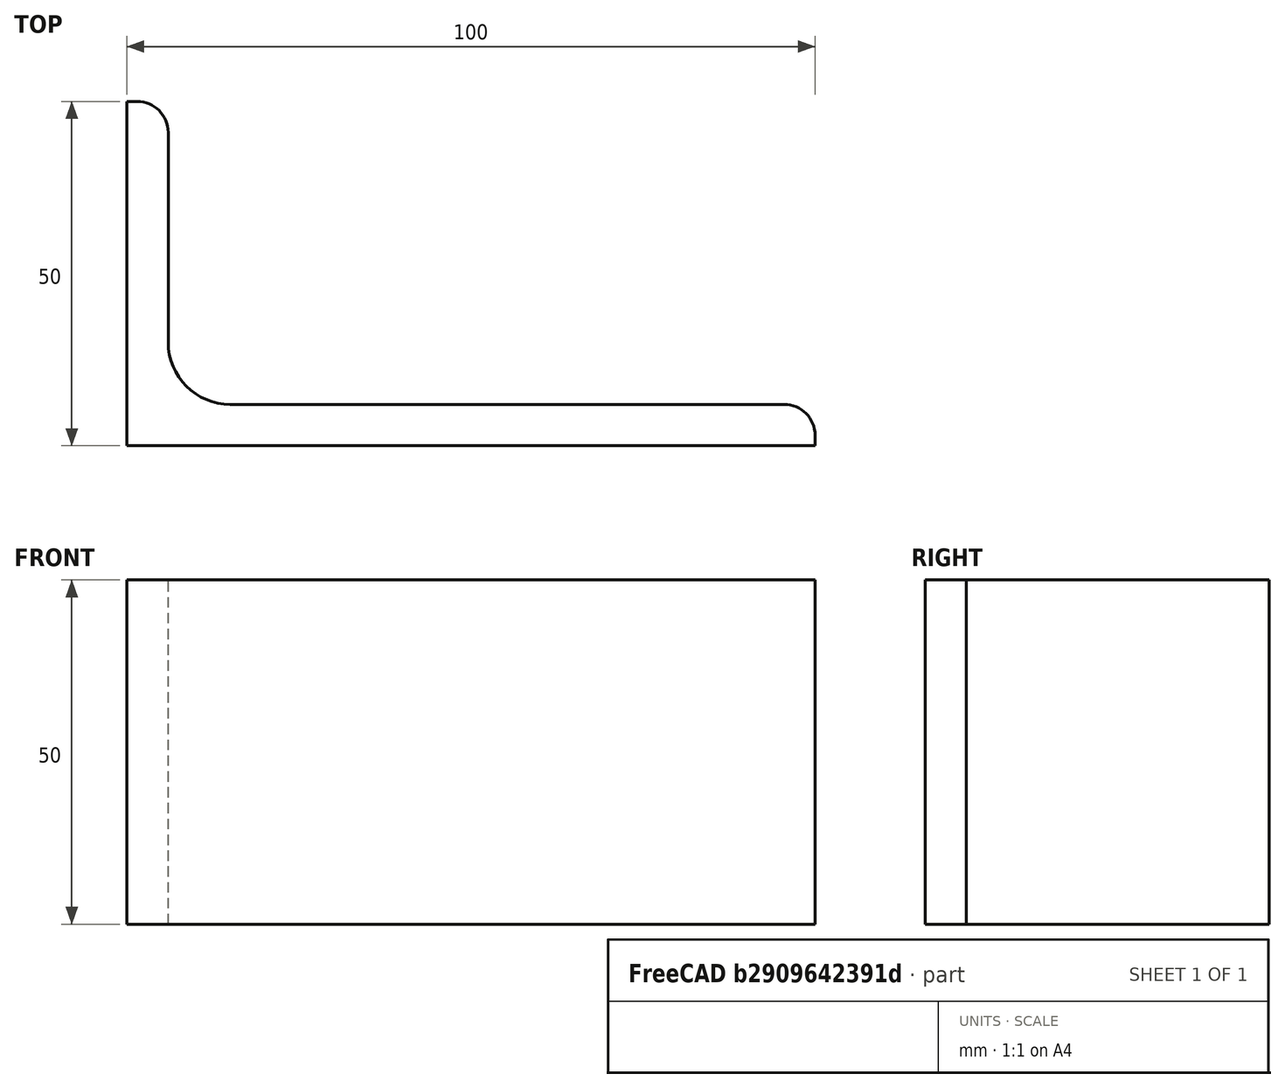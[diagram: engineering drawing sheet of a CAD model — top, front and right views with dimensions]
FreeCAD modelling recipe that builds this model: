
FCSTD DOCUMENT  (FreeCAD 0.15R4671 (Git))
Label: Angle Bar 100x50x6 EN10056 S235JR
License: All rights reserved
LicenseURL: http://en.wikipedia.org/wiki/All_rights_reserved
objects: Sketcher::SketchObject×1, Part::Extrusion×1
note: 2 computed .brp shape members not serialized (recipe doc carries the construction recipe); baked Part::Feature solids carry a one-line shape summary decoded from their .brp

FEATURE [Sketcher::SketchObject] Sketch
  sketch-geometry (9):
    g0: LineSegment StartX=0 StartY=0 StartZ=0 EndX=100 EndY=0 EndZ=0
    g1: LineSegment StartX=100 StartY=0 StartZ=0 EndX=100 EndY=1.5 EndZ=0
    g2: LineSegment StartX=95.5 StartY=6 StartZ=0 EndX=15 EndY=6 EndZ=0
    g3: LineSegment StartX=0 StartY=0 StartZ=0 EndX=0 EndY=50 EndZ=0
    g4: LineSegment StartX=0 StartY=50 StartZ=0 EndX=1.5 EndY=50 EndZ=0
    g5: LineSegment StartX=6 StartY=45.5 StartZ=0 EndX=6 EndY=15 EndZ=0
    g6: ArcOfCircle CenterX=15 CenterY=15 CenterZ=0 NormalX=0 NormalY=0 NormalZ=1 Radius=9 StartAngle=3.14159 EndAngle=4.71239
    g7: ArcOfCircle CenterX=1.5 CenterY=45.5 CenterZ=0 NormalX=0 NormalY=0 NormalZ=1 Radius=4.5 StartAngle=0 EndAngle=1.5708
    g8: ArcOfCircle CenterX=95.5 CenterY=1.5 CenterZ=0 NormalX=0 NormalY=0 NormalZ=1 Radius=4.5 StartAngle=0 EndAngle=1.5708
  constraints (23):
    c: Coincident(g0,g-1)
    c: Horizontal(g0)
    c: Coincident(g1,g0)
    c: Vertical(g1)
    c: Horizontal(g2)
    c: Coincident(g3,g-1)
    c: Vertical(g3)
    c: Coincident(g4,g3)
    c: Horizontal(g4)
    c: Vertical(g5)
    c: Tangent(g5,g6) = -1.5708
    c: Tangent(g2,g6) = 1.5708
    c: Tangent(g4,g7) = 1.5708
    c: Tangent(g5,g7) = 1.5708
    c: Tangent(g2,g8) = -1.5708
    c: Tangent(g1,g8) = -1.5708
    c: DistanceX(g0) = 100
    c: DistanceY(g3) = 50
    c: DistanceY(g0,g2) = 6
    c: DistanceX(g3,g5) = 6
    c: Radius(g6) = 9
    c: Radius(g8) = 4.5
    c: Radius(g7) = 4.5
FEATURE [Part::Extrusion] Extrude  label="Angle Bar 100x50x6 EN10056 S235JR"
  Base = -> Sketch
  Dir = (0,0,50)
  Solid = true
